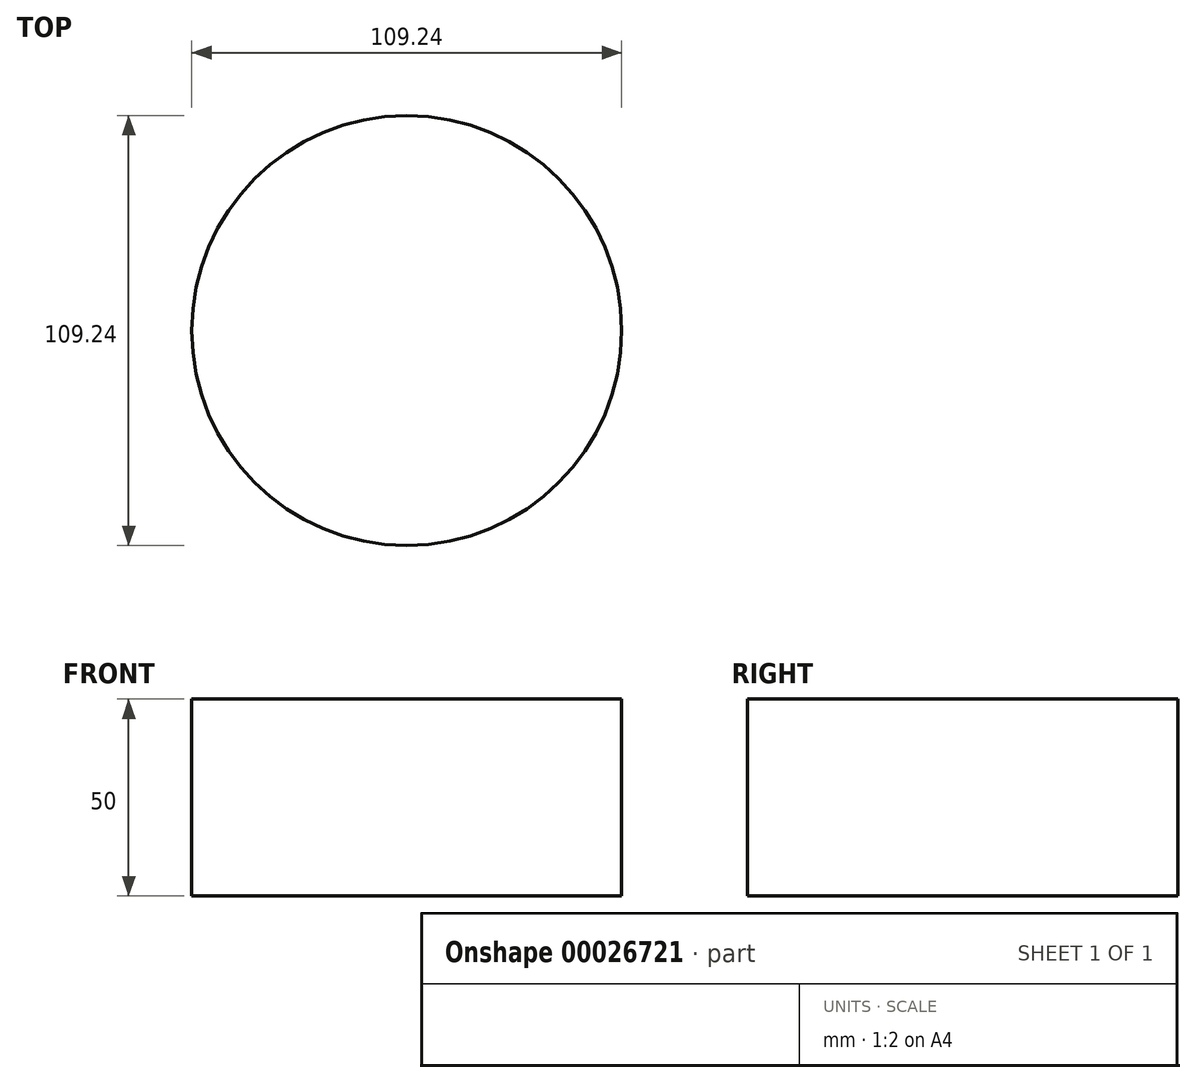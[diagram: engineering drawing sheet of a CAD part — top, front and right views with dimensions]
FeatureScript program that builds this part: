
annotation { "Feature Type Name" : "Feature", "Feature Type Description" : "" }
export const myFeature = defineFeature(function(context is Context, id is Id, definition is map)
    precondition{}
    {
        {
            var Q0;
            Q0=qCreatedBy(makeId("Top.planeOp"),FACE);
            var sketch = newSketch(context, id + "F0", { "sketchPlane" : qUnion([Q0])});
            skCircle(sketch, "E0", {"center": v(0, 0) * mm, "radius": 54.62 * mm});
            skSolve(sketch);
        }
        {
            var Q0;
            Q0=makeQuery(id+"F0.imprint","IMPRINT",FACE,{"disambiguationData":[TD([[makeQuery(id+"F0.imprint","IMPRINT",EDGE,{"derivedFrom":sQuery(id+"F0.wireOp",EDGE,"E0")}),1.0]])]});
            extrude(context, id + "F1", {"entities" : qUnion([Q0]), "depth" : 50 * mm});
        }
    });
